# Revit family: Epure_Evolution_SBU
name_source: partatom
category: Plumbing Fixtures
revit_build: Autodesk Revit Architecture 2012 (Build: 20110916_2132(x64)
units: mm (PartAtom-declared; Revit-internal decimal feet)

## types (1)
- Evolution Single Bowl Undermount - 0TH
    CW Connection = No
    Cost = 0 $
    Default Elevation = 1219 mm
    Depth_ANZRS = 440 mm  [stored 1.44357 ft]
    Description = Evolution Single Bowl Undermount - 0TH
    HW Connection = No
    Height_ANZRS = 200 mm  [stored 0.656168 ft]
    Manufacturer = Caroma
    Model = EVOSBU
    Tub_ANZRS = Chrome_Caroma
    Type Comments = Evolution Single Bowl Undermount - 0TH
    URL = http://www.epure.com.au
    Vent Connection = No
    Waste Connection = Yes
    Width_ANZRS = 380 mm

note: [stored X ft] marks values corroborated as IEEE doubles in the binary element streams (Revit-internal decimal feet)

## geometry (parser evidence)
native form markers: Blend x1, Sweep x4
no freeform markers — native parametric forms only
